# Revit family: Electronics_Interfaces_Biamp_Vocia_Enhanced-Life-Safety_LSI-16e__
name_source: partatom
category: Communication Devices
units: mm (PartAtom-declared; Revit-internal decimal feet)

## family parameters
Cut with Voids When Loaded = No
Host = Face
Maintain Annotation Orientation = No
OmniClass Number = 23.85.10.11.11
OmniClass Title = Sound and Signal Devices
Part Type = Normal
Room Calculation Point = No
Round Connector Dimension = Use Diameter
Shared = No

## types (1)
- LSI-16e
    Altitude = 0-10,000 ft (0-3000m) MSL
    Apparent Load = 15 VA
    Baud Rate = 57600
    Compliance = EN 54-16 certified, FCC Part 15B (USA). CE marked (Europe), RoHS Directive (Europe), RINA (Italy), EN 60849, AS 60849 verified
    Connector Description = 24V DC 15W
    Current Limit = 0.8A
    Default Elevation = 48 "
    Depth = 10 "
    Description = Vocia® LSI-16e Enhanced Life Safety Interface
    Height = 1.75 "
    High Range Hysteresis = 1V ± 20%
    High Range Logic High = 12-30VDC
    High Range Logic Low = 0-11VDC
    Housing Material = Biamp - Metal - Silver
    Humidity = 0-95% relative humidity (non-condensing)
    Input Isolation = 500V RMS (isolation from LSI-16)
    Input Transient Protection = ± 8kV peak
    Isolation = 3kV
    Load = Resistive
    Manufacturer = Biamp
    Max Continuous Current = 0.35A
    Max Operating Current = 600mA AC, 1A DC
    Max Operating Voltage = 125VAC, 60VDC
    Max Power Consumption = 15 W
    Max Sink Current = 6mA
    Max Switching Capacity = 37.5VA, 30W
    Maximum External Supply = 35V
    Min Sink Current = 1mA
    Min permissible load = 10 μA at 10mVDC
    Model = Vocia LSI-16e
    Network Connection = RJ-45 with shielded Ethernet, (CAT5, CAT5e, CAT6 or CAT7)
    Number Control Inputs = Eight
    Number General Purpose Inputs = 16
    Number Monitored I/O = Eight
    Number of Poles = 1
    Power Factor = 1
    Product Documentation Link = https://downloads.biamp.com
    Product Page URL = https://www.biamp.com
    Product data url = https://www.bimobject.com
    TTL Hysteresis = 1V ± 20%
    TTL Logic High = 2-5V
    TTL Logic Low = 0-0.8V
    Temperature Range = 23 - 104° F (-5 - 40° C)
    Type Control Inputs = Opto Isolator LED
    Type Monitored I/O = FET switch, open drain, (low side driver)
    Type RS232 Port = DTE
    Type System Fault Relay = Single Form C voltage-free SPST change-over contact
    URL = https://www.biamp.com
    VMon Input Shutdown = 35V
    Vocia LSI = Yes
    Voltage = 24 V
    Weight = 6.40 lbf
    Width = 19 "

## geometry (parser evidence)
native form markers: Sweep x2
no freeform markers — native parametric forms only
